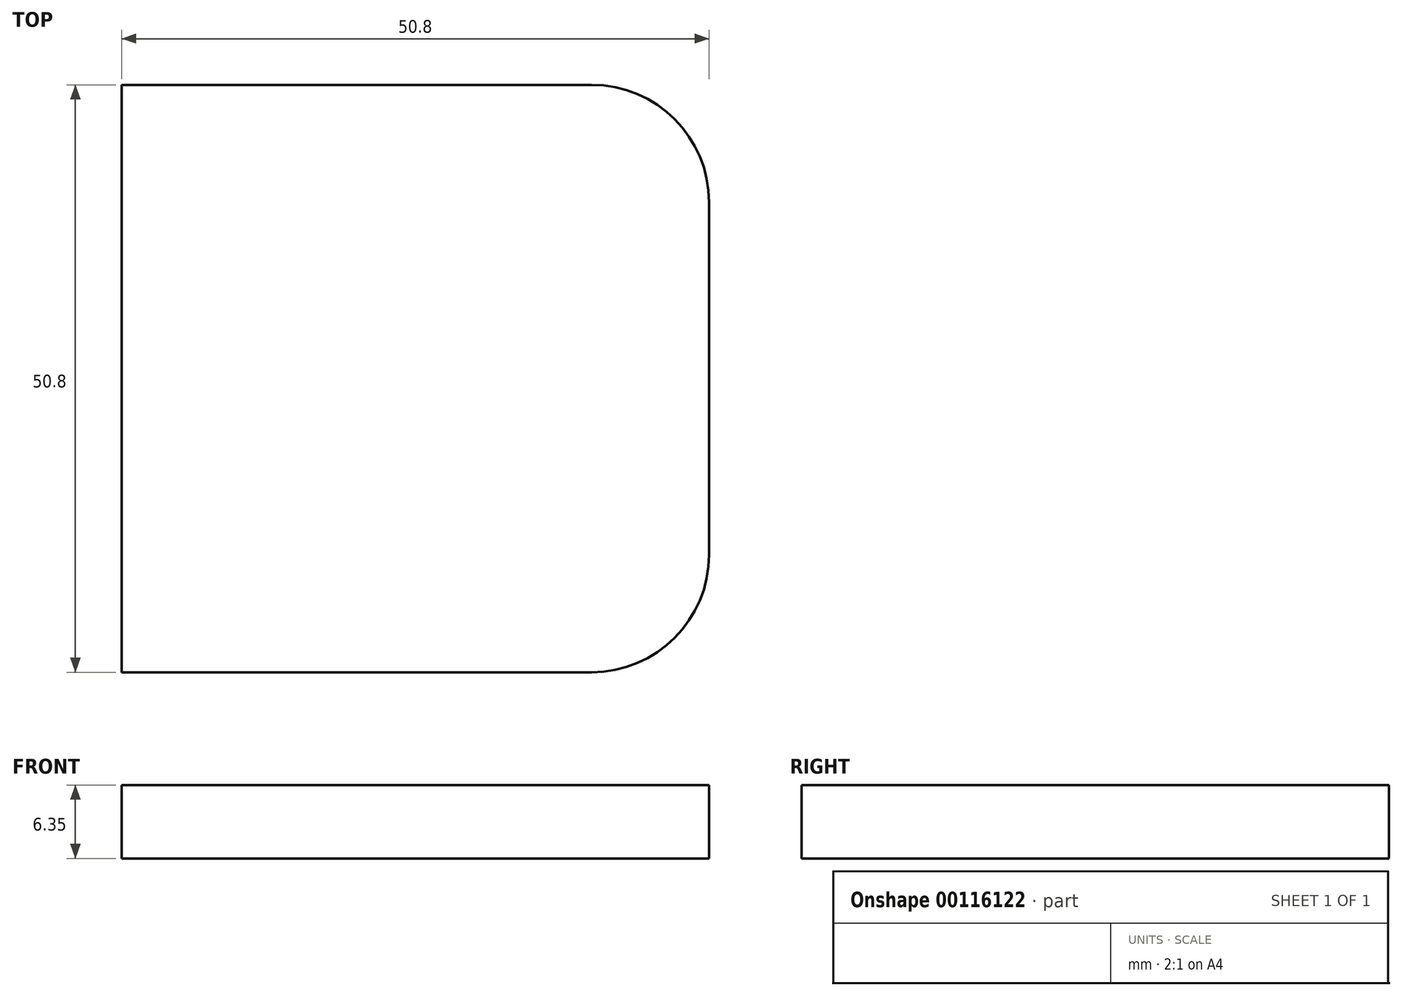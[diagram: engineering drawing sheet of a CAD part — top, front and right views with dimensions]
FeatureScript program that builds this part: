
annotation { "Feature Type Name" : "Feature", "Feature Type Description" : "" }
export const myFeature = defineFeature(function(context is Context, id is Id, definition is map)
    precondition{}
    {
        {
            var Q0;
            Q0=qCreatedBy(makeId("Top.planeOp"),FACE);
            var sketch = newSketch(context, id + "F0", { "sketchPlane" : qUnion([Q0])});
            skLineSegment(sketch, "E0.bottom", {"start": v(0, 0) * mm, "end": v(40.64, 0) * mm});
            skLineSegment(sketch, "E0.top", {"start": v(0, -50.8) * mm, "end": v(40.64, -50.8) * mm});
            skLineSegment(sketch, "E0.left", {"start": v(0, 0) * mm, "end": v(0, -50.8) * mm});
            skLineSegment(sketch, "E0.right", {"start": v(50.8, -10.16) * mm, "end": v(50.8, -40.64) * mm});
            skPoint(sketch, "E1.visualSharp", {"position": v(50.8, 0) * mm});
            skArc(sketch, "E1.filletArc", {"start": v(50.8, -10.16) * mm, "mid": v(47.82, -2.98) * mm, "end": v(40.64, 0) * mm});
            skPoint(sketch, "E2.visualSharp", {"position": v(50.8, -50.8) * mm});
            skArc(sketch, "E2.filletArc", {"start": v(40.64, -50.8) * mm, "mid": v(47.82, -47.82) * mm, "end": v(50.8, -40.64) * mm});
            skSolve(sketch);
        }
        {
            var Q0;
            Q0=makeQuery(id+"F0.imprint","IMPRINT",FACE,{"disambiguationData":[TD([[makeQuery(id+"F0.imprint","IMPRINT",EDGE,{"derivedFrom":sQuery(id+"F0.wireOp",EDGE,"E0.bottom")}),-1.0]])]});
            extrude(context, id + "F1", {"entities" : qUnion([Q0]), "depth" : 6.35 * mm});
        }
    });
